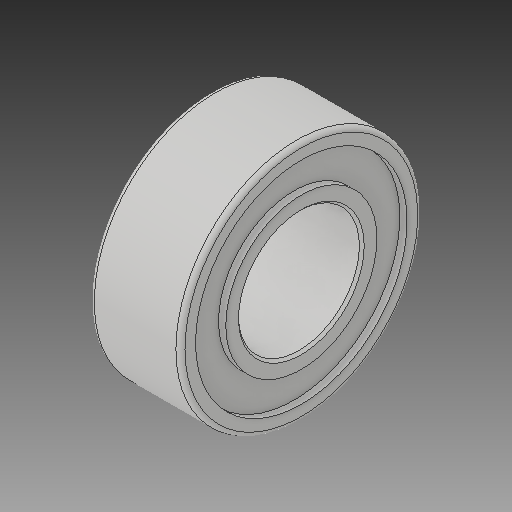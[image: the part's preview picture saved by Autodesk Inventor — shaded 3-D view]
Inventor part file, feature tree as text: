
AUTODESK INVENTOR PART (.ipt)
format: ipt  version: 2018 (Build 220112000, 112)  size: 168,960 bytes
history: native  units: in
note: dims shown in document units (in); Inventor stores cm internally (conversion verified against a paired STEP export)
features: chamfer x1
ambient origin geometry x8: Origin, YZ Plane, XZ Plane, XY Plane, X Axis, Y Axis, Z Axis, Center Point
bodies: Solid1 (feature_tree)
feature tree (1):
  chamfer  "Chamfer1"  [1 undecoded]
note: 1 required parameter value undecoded (feature->parameter linkage not recoverable at this tier; creation-order binding heuristic only, values carry confidence <= 0.55)
